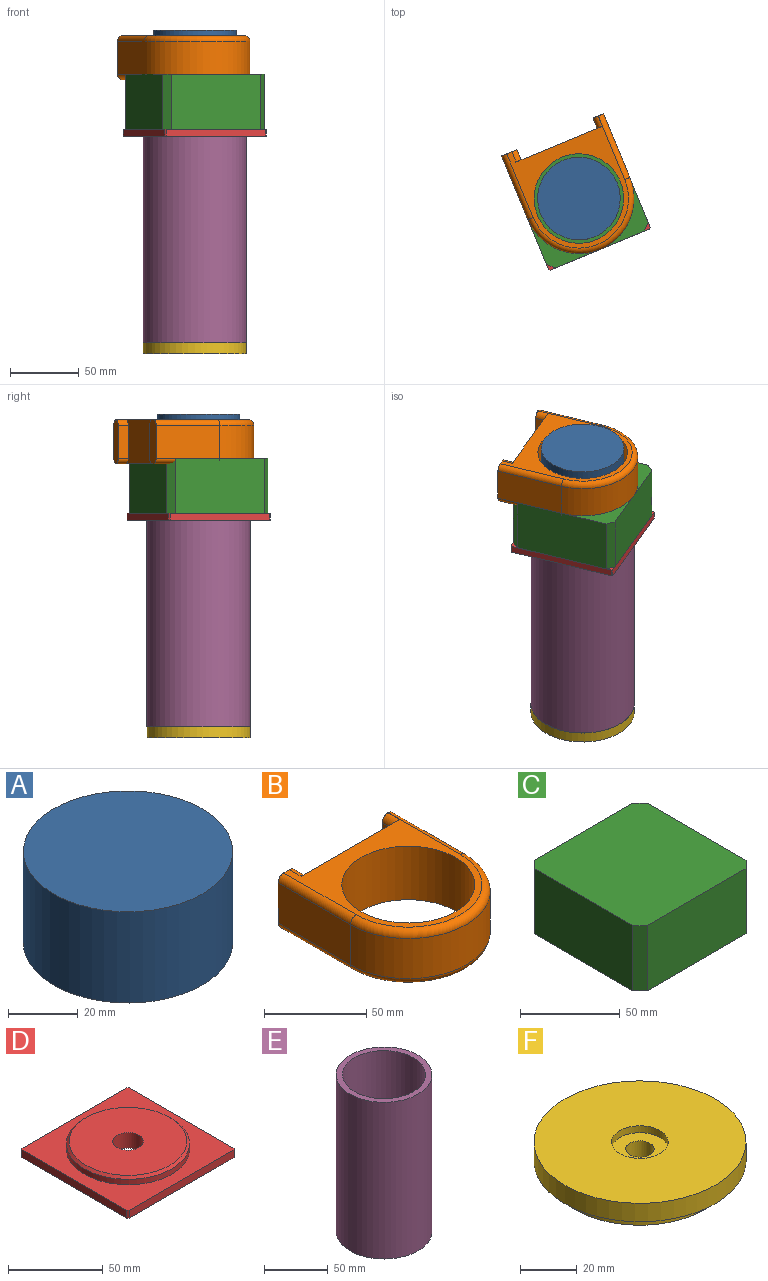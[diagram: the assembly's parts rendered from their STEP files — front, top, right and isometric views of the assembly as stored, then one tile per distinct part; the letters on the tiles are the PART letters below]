
ASSEMBLY  parts=6 mates=5
PART A: 3 faces, bbox 60x60x32 mm
  f0: cylinder r=30mm len=60mm, axis (0,0,1), area 6031.9mm2, adj f1,f2
  f1: plane 60x60mm, normal (0,0,-1), area 2827.4mm2, adj f0
  f2: plane 60x60mm, normal (0,0,1), area 2827.4mm2, adj f0
PART B: 21 faces, bbox 86.6x93.3x32 mm
  f0: plane 32x8.07mm, normal (0,1,0), area 244.4mm2, adj f1,f4,f7,f8,f11,f14,f17,f20
  f1: plane 86x72mm, normal (0,0,1), area 1773.4mm2, adj f0,f5,f6,f10,f14,f15,f16,f19
  f2: plane 50x24mm, normal (-1,0,0), area 1200mm2, adj f3,f5,f13,f16
  f3: cylinder r=40mm len=80mm, axis (0,0,-1), area 3015.9mm2, adj f2,f4,f12,f15
  f4: plane 50x24mm, normal (1,0,0), area 1200mm2, adj f0,f3,f11,f14
  f5: plane 32x11.93mm, normal (0,1,0), area 368.1mm2, adj f1,f2,f7,f9,f13,f16,f18,f19
  f6: cylinder r=32.5mm len=65mm, axis (0,0,-1), area 6534.5mm2, adj f1,f7
  f7: plane 86x72mm, normal (0,0,-1), area 1773.4mm2, adj f0,f5,f6,f10,f11,f12,f13,f17
  f8: plane 24x8mm, normal (-1,0,0), area 192mm2, adj f0,f10,f17,f20
  f9: plane 24x8mm, normal (1,0,0), area 192mm2, adj f5,f10,f18,f19
  f10: plane 68x32mm, normal (0,1,0), area 1933.7mm2, adj f1,f7,f8,f9,f17,f18,f19,f20
  f11: cylinder r=4mm len=50mm, axis (0,1,0), area 314.2mm2, adj f0,f4,f7,f12
  f12: torus R=36mm, axis (0,0,1), area 760.9mm2, adj f3,f7,f11,f13
  f13: cylinder r=4mm len=50mm, axis (0,-1,0), area 314.2mm2, adj f2,f5,f7,f12
  f14: cylinder r=4mm len=50mm, axis (0,-1,0), area 314.2mm2, adj f0,f1,f4,f15
  f15: torus R=36mm, axis (0,0,1), area 760.9mm2, adj f1,f3,f14,f16
  f16: cylinder r=4mm len=50mm, axis (0,1,0), area 314.2mm2, adj f1,f2,f5,f15
  f17: cylinder r=4mm len=8mm, axis (0,-1,0), area 50.3mm2, adj f0,f7,f8,f10
  f18: cylinder r=4mm len=8mm, axis (0,1,0), area 50.3mm2, adj f5,f7,f9,f10
  f19: cylinder r=4mm len=8mm, axis (0,-1,0), area 50.3mm2, adj f1,f5,f9,f10
  f20: cylinder r=4mm len=8mm, axis (0,1,0), area 50.3mm2, adj f0,f1,f8,f10
PART C: 10 faces, bbox 80x80x40 mm
  f0: plane 70x40mm, normal (1,0,0), area 2800mm2, adj f4,f5,f8,f9
  f1: plane 70x40mm, normal (0,1,0), area 2800mm2, adj f4,f5,f6,f8
  f2: plane 70x40mm, normal (-1,0,0), area 2800mm2, adj f4,f5,f6,f7
  f3: plane 70x40mm, normal (0,-1,0), area 2800mm2, adj f4,f5,f7,f9
  f4: plane 80x80mm, normal (0,0,-1), area 6350mm2, adj f0,f1,f2,f3,f6,f7,f8,f9
  f5: plane 80x80mm, normal (0,0,1), area 6350mm2, adj f0,f1,f2,f3,f6,f7,f8,f9
  f6: plane 40x5mm, normal (-0.71,0.71,0), area 282.8mm2, adj f1,f2,f4,f5
  f7: plane 40x5mm, normal (-0.71,-0.71,0), area 282.8mm2, adj f2,f3,f4,f5
  f8: plane 40x5mm, normal (0.71,0.71,0), area 282.8mm2, adj f0,f1,f4,f5
  f9: plane 40x5mm, normal (0.71,-0.71,0), area 282.8mm2, adj f0,f3,f4,f5
PART D: 14 faces, bbox 80x80x10 mm
  f0: plane 78x5mm, normal (1,0,0), area 390mm2, adj f4,f5,f10,f12
  f1: plane 78x5mm, normal (0,1,0), area 390mm2, adj f4,f5,f12,f13
  f2: plane 78x5mm, normal (-1,0,0), area 390mm2, adj f4,f5,f11,f13
  f3: plane 78x5mm, normal (0,-1,0), area 390mm2, adj f4,f5,f10,f11
  f4: plane 80x80mm, normal (0,0,-1), area 6196.9mm2, adj f0,f1,f2,f3,f8,f10,f11,f12
  f5: plane 80x80mm, normal (0,0,1), area 3079.7mm2, adj f0,f1,f2,f3,f6,f10,f11,f12
  f6: cylinder r=32.5mm len=65mm, axis (0,0,-1), area 714.7mm2, adj f5,f9
  f7: plane 62x62mm, normal (0,0,1), area 2818mm2, adj f8,f9
  f8: cylinder r=8mm len=16mm, axis (0,0,1), area 502.7mm2, adj f4,f7
  f9: cone r=31mm half-angle=45deg, axis (0,0,-1), area 423.2mm2, adj f6,f7
  f10: plane 5x1mm, normal (0.71,-0.71,0), area 7.1mm2, adj f0,f3,f4,f5
  f11: plane 5x1mm, normal (-0.71,-0.71,0), area 7.1mm2, adj f2,f3,f4,f5
  f12: plane 5x1mm, normal (0.71,0.71,0), area 7.1mm2, adj f0,f1,f4,f5
  f13: plane 5x1mm, normal (-0.71,0.71,0), area 7.1mm2, adj f1,f2,f4,f5
PART E: 4 faces, bbox 75x75x150 mm
  f0: cylinder r=37.5mm len=150mm, axis (0,0,-1), area 35342.9mm2, adj f2,f3
  f1: cylinder r=32.5mm len=150mm, axis (0,0,-1), area 30630.5mm2, adj f2,f3
  f2: plane 75x75mm, normal (0,0,1), area 1099.6mm2, adj f0,f1
  f3: plane 75x75mm, normal (0,0,-1), area 1099.6mm2, adj f0,f1
PART F: 8 faces, bbox 75x75x13 mm
  f0: plane 75x75mm, normal (0,0,1), area 4103.7mm2, adj f1,f5
  f1: cylinder r=37.5mm len=75mm, axis (0,0,-1), area 1885mm2, adj f0,f2
  f2: plane 75x75mm, normal (0,0,-1), area 1099.6mm2, adj f1,f3
  f3: cylinder r=32.5mm len=65mm, axis (0,0,-1), area 1021mm2, adj f2,f4
  f4: plane 65x65mm, normal (0,0,-1), area 3239.8mm2, adj f3,f7
  f5: cylinder r=10mm len=20mm, axis (0,0,1), area 188.5mm2, adj f0,f6
  f6: plane 20x20mm, normal (0,0,1), area 235.6mm2, adj f5,f7
  f7: cylinder r=5mm len=10mm, axis (0,0,1), area 314.2mm2, adj f4,f6
PLACE A rot(axis=(-0.56,-0.83,0),180deg) t=(34.16,54.15,-97.55)mm
PLACE B rot(axis=(0,0,1),22.5deg) t=(34.16,54.15,-101.55)mm
PLACE C rot(axis=(0.98,0.2,0),180deg) t=(34.16,54.15,-137.55)mm fixed
PLACE D rot(axis=(0.2,-0.98,0),180deg) t=(34.16,54.15,-142.55)mm
PLACE E rot(axis=(0.2,-0.98,0),180deg) t=(34.16,54.15,-217.55)mm
PLACE F rot(axis=(0.2,-0.98,0),180deg) t=(34.16,54.15,-292.55)mm
MATE fastened C.f5 <-> D.f8  axis (0,0,-1) through (34.16,54.15,-137.55)mm
MATE fastened A.f0 <-> B.f3  axis (0,0,-1) through (34.16,54.15,-97.55)mm
MATE fastened E.f0 <-> F.f1  axis (0,0,-1) through (34.16,54.15,-292.55)mm
MATE fastened D.f8 <-> E.f0  axis (0,0,-1) through (34.16,54.15,-142.55)mm
MATE fastened A.f0 <-> C.f4  axis (0,0,-1) through (34.16,54.15,-97.55)mm
